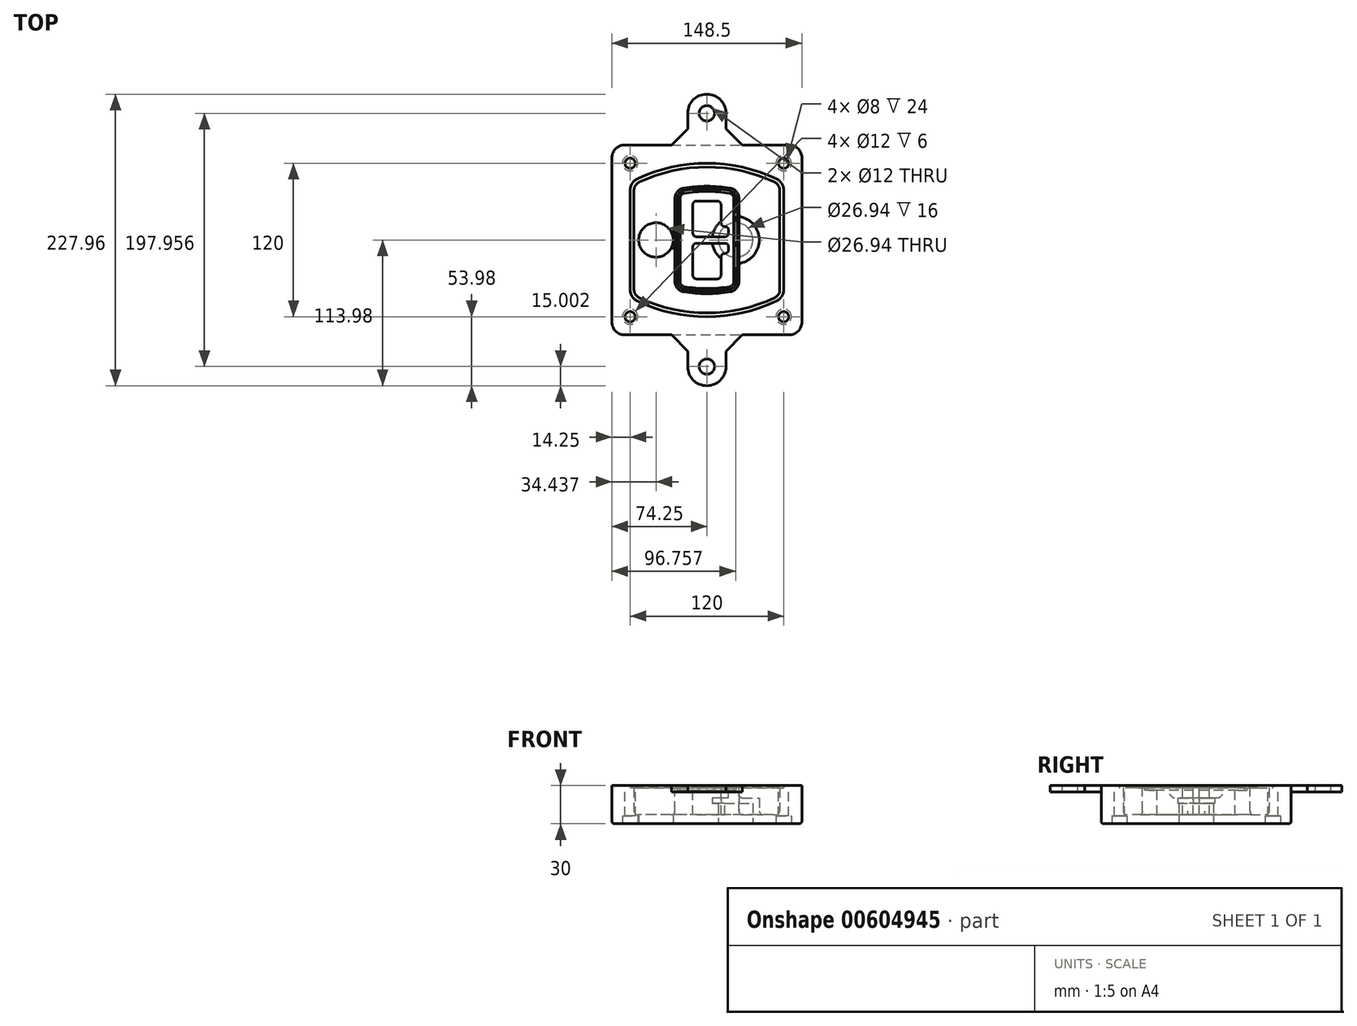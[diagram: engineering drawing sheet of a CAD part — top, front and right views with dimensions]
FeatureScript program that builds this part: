
annotation { "Feature Type Name" : "Feature", "Feature Type Description" : "" }
export const myFeature = defineFeature(function(context is Context, id is Id, definition is map)
    precondition{}
    {
        {
            var Q0;
            Q0=qCreatedBy(makeId("Top.planeOp"),FACE);
            var sketch = newSketch(context, id + "F0", { "sketchPlane" : qUnion([Q0])});
            skPoint(sketch, "E0.rect.middle", {"position": v(0, 0) * mm});
            skLineSegment(sketch, "E1.bottom", {"start": v(-64.25, -74.25) * mm, "end": v(64.25, -74.25) * mm});
            skLineSegment(sketch, "E1.top", {"start": v(-64.25, 74.25) * mm, "end": v(64.25, 74.25) * mm});
            skLineSegment(sketch, "E1.left", {"start": v(-74.25, -64.25) * mm, "end": v(-74.25, 64.25) * mm});
            skLineSegment(sketch, "E1.right", {"start": v(74.25, -64.25) * mm, "end": v(74.25, 64.25) * mm});
            skLineSegment(sketch, "E2", {"start": v(-74.25, 74.25) * mm, "end": v(74.25, -74.25) * mm, "construction": true});
            skLineSegment(sketch, "E3", {"start": v(74.25, 74.25) * mm, "end": v(-74.25, -74.25) * mm, "construction": true});
            skCircle(sketch, "E4", {"center": v(-60, 60) * mm, "radius": 4 * mm});
            skCircle(sketch, "E5", {"center": v(60, 60) * mm, "radius": 4 * mm});
            skCircle(sketch, "E6", {"center": v(60, -60) * mm, "radius": 4 * mm});
            skCircle(sketch, "E7", {"center": v(-60, -60) * mm, "radius": 4 * mm});
            skLineSegment(sketch, "E8", {"start": v(-60, 60) * mm, "end": v(60, 60) * mm, "construction": true});
            skLineSegment(sketch, "E9", {"start": v(60, 60) * mm, "end": v(60, -60) * mm, "construction": true});
            skLineSegment(sketch, "E10", {"start": v(60, -60) * mm, "end": v(-60, -60) * mm, "construction": true});
            skLineSegment(sketch, "E11", {"start": v(-60, -60) * mm, "end": v(-60, 60) * mm, "construction": true});
            skLineSegment(sketch, "E12", {"start": v(-60, 38.83) * mm, "end": v(-60, -38.83) * mm});
            skLineSegment(sketch, "E13", {"start": v(60, 38.83) * mm, "end": v(60, -38.83) * mm});
            skArc(sketch, "E14", {"start": v(54.26, 47.88) * mm, "mid": v(0, 60) * mm, "end": v(-54.26, 47.88) * mm});
            skArc(sketch, "E15", {"start": v(-54.26, -47.88) * mm, "mid": v(0, -60) * mm, "end": v(54.26, -47.88) * mm});
            skLineSegment(sketch, "E16", {"start": v(-60, 0) * mm, "end": v(60, 0) * mm, "construction": true});
            skPoint(sketch, "E17.visualSharp", {"position": v(-60, -45) * mm});
            skArc(sketch, "E17.filletArc", {"start": v(-60, -38.83) * mm, "mid": v(-58.44, -44.2) * mm, "end": v(-54.26, -47.88) * mm});
            skPoint(sketch, "E18.visualSharp", {"position": v(-60, 45) * mm});
            skArc(sketch, "E18.filletArc", {"start": v(-54.26, 47.88) * mm, "mid": v(-58.44, 44.2) * mm, "end": v(-60, 38.83) * mm});
            skPoint(sketch, "E19.visualSharp", {"position": v(60, 45) * mm});
            skArc(sketch, "E19.filletArc", {"start": v(60, 38.83) * mm, "mid": v(58.44, 44.2) * mm, "end": v(54.26, 47.88) * mm});
            skPoint(sketch, "E20.visualSharp", {"position": v(60, -45) * mm});
            skArc(sketch, "E20.filletArc", {"start": v(54.26, -47.88) * mm, "mid": v(58.44, -44.2) * mm, "end": v(60, -38.83) * mm});
            skPoint(sketch, "E21.visualSharp", {"position": v(-74.25, 74.25) * mm});
            skArc(sketch, "E21.filletArc", {"start": v(-64.25, 74.25) * mm, "mid": v(-71.32, 71.32) * mm, "end": v(-74.25, 64.25) * mm});
            skPoint(sketch, "E22.visualSharp", {"position": v(74.25, 74.25) * mm});
            skArc(sketch, "E22.filletArc", {"start": v(74.25, 64.25) * mm, "mid": v(71.32, 71.32) * mm, "end": v(64.25, 74.25) * mm});
            skPoint(sketch, "E23.visualSharp", {"position": v(74.25, -74.25) * mm});
            skArc(sketch, "E23.filletArc", {"start": v(64.25, -74.25) * mm, "mid": v(71.32, -71.32) * mm, "end": v(74.25, -64.25) * mm});
            skPoint(sketch, "E24.visualSharp", {"position": v(-74.25, -74.25) * mm});
            skArc(sketch, "E24.filletArc", {"start": v(-74.25, -64.25) * mm, "mid": v(-71.32, -71.32) * mm, "end": v(-64.25, -74.25) * mm});
            skArc(sketch, "E25.0", {"start": v(57, 38.83) * mm, "mid": v(55.9, 42.58) * mm, "end": v(52.98, 45.17) * mm});
            skLineSegment(sketch, "E25.1", {"start": v(57, 38.83) * mm, "end": v(57, -38.83) * mm});
            skArc(sketch, "E25.2", {"start": v(52.98, -45.17) * mm, "mid": v(55.9, -42.58) * mm, "end": v(57, -38.83) * mm});
            skArc(sketch, "E25.3", {"start": v(-52.98, -45.17) * mm, "mid": v(0, -57) * mm, "end": v(52.98, -45.17) * mm});
            skArc(sketch, "E25.4", {"start": v(-57, -38.83) * mm, "mid": v(-55.9, -42.58) * mm, "end": v(-52.98, -45.17) * mm});
            skArc(sketch, "E25.5", {"start": v(52.98, 45.17) * mm, "mid": v(0, 57) * mm, "end": v(-52.98, 45.17) * mm});
            skLineSegment(sketch, "E25.6", {"start": v(-57, 38.83) * mm, "end": v(-57, -38.83) * mm});
            skArc(sketch, "E25.7", {"start": v(-52.98, 45.17) * mm, "mid": v(-55.9, 42.58) * mm, "end": v(-57, 38.83) * mm});
            skArc(sketch, "E26.0", {"start": v(-55.96, 51.5) * mm, "mid": v(-61.82, 46.33) * mm, "end": v(-64, 38.83) * mm});
            skArc(sketch, "E26.1", {"start": v(55.96, 51.5) * mm, "mid": v(0, 64) * mm, "end": v(-55.96, 51.5) * mm});
            skArc(sketch, "E26.2", {"start": v(64, 38.83) * mm, "mid": v(61.82, 46.33) * mm, "end": v(55.96, 51.5) * mm});
            skLineSegment(sketch, "E26.3", {"start": v(64, 38.83) * mm, "end": v(64, -38.83) * mm});
            skArc(sketch, "E26.4", {"start": v(55.96, -51.5) * mm, "mid": v(61.82, -46.33) * mm, "end": v(64, -38.83) * mm});
            skLineSegment(sketch, "E26.5", {"start": v(-64, 38.83) * mm, "end": v(-64, -38.83) * mm});
            skArc(sketch, "E26.6", {"start": v(-55.96, -51.5) * mm, "mid": v(0, -64) * mm, "end": v(55.96, -51.5) * mm});
            skArc(sketch, "E26.7", {"start": v(-64, -38.83) * mm, "mid": v(-61.82, -46.33) * mm, "end": v(-55.96, -51.5) * mm});
            skSolve(sketch);
        }
        {
            var Q0;
            Q0=makeQuery(id+"F0.imprint","IMPRINT",FACE,{"disambiguationData":[TD([[makeQuery(id+"F0.imprint","IMPRINT",EDGE,{"derivedFrom":sQuery(id+"F0.wireOp",EDGE,"E1.bottom")}),1.0]])]});
            var Q1;
            Q1=makeQuery(id+"F0.imprint","IMPRINT",FACE,{"disambiguationData":[TD([[makeQuery(id+"F0.imprint","IMPRINT",EDGE,{"derivedFrom":sQuery(id+"F0.wireOp",EDGE,"E12")}),1.0]])]});
            var Q2;
            Q2=makeQuery(id+"F0.imprint","IMPRINT",FACE,{"disambiguationData":[TD([[makeQuery(id+"F0.imprint","IMPRINT",EDGE,{"derivedFrom":sQuery(id+"F0.wireOp",EDGE,"E25.0")}),1.0]])]});
            var Q3;
            Q3=makeQuery(id+"F0.imprint","IMPRINT",FACE,{"disambiguationData":[TD([[makeQuery(id+"F0.imprint","IMPRINT",EDGE,{"derivedFrom":sQuery(id+"F0.wireOp",EDGE,"E12")}),-1.0]])]});
            extrude(context, id + "F1", {"entities" : qUnion([Q0, Q1, Q2, Q3]), "oppositeDirection" : true, "depth" : 25 * mm});
        }
        {
            var Q0;
            Q0=makeQuery(id+"F0.imprint","IMPRINT",FACE,{"disambiguationData":[TD([[makeQuery(id+"F0.imprint","IMPRINT",EDGE,{"derivedFrom":sQuery(id+"F0.wireOp",EDGE,"E12")}),1.0]])]});
            extrude(context, id + "F2", {"entities" : qUnion([Q0]), "operationType" : NewBodyOperationType.ADD, "depth" : 3 * mm});
        }
        {
            var Q0;
            Q0=makeQuery(id+"F0.imprint","IMPRINT",FACE,{"disambiguationData":[TD([[makeQuery(id+"F0.imprint","IMPRINT",EDGE,{"derivedFrom":sQuery(id+"F0.wireOp",EDGE,"E25.0")}),1.0]])]});
            extrude(context, id + "F3", {"entities" : qUnion([Q0]), "operationType" : NewBodyOperationType.REMOVE, "oppositeDirection" : true, "depth" : 18 * mm});
        }
        {
            var Q0;
            Q0=makeQuery(id+"F2.opExtrude","CAP_FACE",FACE,{"disambiguationData":[OSD([sQuery(id+"F0.wireOp",EDGE,"E12"),sQuery(id+"F0.wireOp",EDGE,"E13"),sQuery(id+"F0.wireOp",EDGE,"E14"),sQuery(id+"F0.wireOp",EDGE,"E15"),sQuery(id+"F0.wireOp",EDGE,"E17.filletArc"),sQuery(id+"F0.wireOp",EDGE,"E18.filletArc"),sQuery(id+"F0.wireOp",EDGE,"E19.filletArc"),sQuery(id+"F0.wireOp",EDGE,"E20.filletArc"),sQuery(id+"F0.wireOp",EDGE,"E25.0"),sQuery(id+"F0.wireOp",EDGE,"E25.1"),sQuery(id+"F0.wireOp",EDGE,"E25.2"),sQuery(id+"F0.wireOp",EDGE,"E25.3"),sQuery(id+"F0.wireOp",EDGE,"E25.4"),sQuery(id+"F0.wireOp",EDGE,"E25.5"),sQuery(id+"F0.wireOp",EDGE,"E25.6"),sQuery(id+"F0.wireOp",EDGE,"E25.7")])],"isStart":false});
            var sketch = newSketch(context, id + "F4", { "sketchPlane" : qUnion([Q0])});
            skArc(sketch, "E27.0", {"start": v(-18.34, -40.45) * mm, "mid": v(0, -42) * mm, "end": v(18.34, -40.45) * mm});
            skArc(sketch, "E28.0", {"start": v(18.34, 40.45) * mm, "mid": v(0, 42) * mm, "end": v(-18.34, 40.45) * mm});
            skLineSegment(sketch, "E29", {"start": v(-25, 32.57) * mm, "end": v(-25, -32.57) * mm});
            skLineSegment(sketch, "E30", {"start": v(25, 32.57) * mm, "end": v(25, -32.57) * mm});
            skLineSegment(sketch, "E31", {"start": v(-25, 39.1) * mm, "end": v(25, 39.1) * mm, "construction": true});
            skLineSegment(sketch, "E32", {"start": v(-25, -39.1) * mm, "end": v(25, -39.1) * mm, "construction": true});
            skPoint(sketch, "E33.visualSharp", {"position": v(-25, 39.1) * mm});
            skArc(sketch, "E33.filletArc", {"start": v(-18.34, 40.45) * mm, "mid": v(-23.11, 37.73) * mm, "end": v(-25, 32.57) * mm});
            skPoint(sketch, "E34.visualSharp", {"position": v(25, 39.1) * mm});
            skArc(sketch, "E34.filletArc", {"start": v(25, 32.57) * mm, "mid": v(23.11, 37.73) * mm, "end": v(18.34, 40.45) * mm});
            skPoint(sketch, "E35.visualSharp", {"position": v(25, -39.1) * mm});
            skArc(sketch, "E35.filletArc", {"start": v(18.34, -40.45) * mm, "mid": v(23.11, -37.73) * mm, "end": v(25, -32.57) * mm});
            skPoint(sketch, "E36.visualSharp", {"position": v(-25, -39.1) * mm});
            skArc(sketch, "E36.filletArc", {"start": v(-25, -32.57) * mm, "mid": v(-23.11, -37.73) * mm, "end": v(-18.34, -40.45) * mm});
            skArc(sketch, "E37.0", {"start": v(52.98, 45.17) * mm, "mid": v(0, 57) * mm, "end": v(-52.98, 45.17) * mm});
            skArc(sketch, "E37.1", {"start": v(-52.98, 45.17) * mm, "mid": v(-55.9, 42.58) * mm, "end": v(-57, 38.83) * mm});
            skLineSegment(sketch, "E37.2", {"start": v(-57, 38.83) * mm, "end": v(-57, -38.83) * mm});
            skArc(sketch, "E37.3", {"start": v(-57, -38.83) * mm, "mid": v(-55.9, -42.58) * mm, "end": v(-52.98, -45.17) * mm});
            skArc(sketch, "E37.4", {"start": v(-52.98, -45.17) * mm, "mid": v(0, -57) * mm, "end": v(52.98, -45.17) * mm});
            skArc(sketch, "E37.5", {"start": v(52.98, -45.17) * mm, "mid": v(55.9, -42.58) * mm, "end": v(57, -38.83) * mm});
            skLineSegment(sketch, "E37.6", {"start": v(57, 38.83) * mm, "end": v(57, -38.83) * mm});
            skArc(sketch, "E37.7", {"start": v(57, 38.83) * mm, "mid": v(55.9, 42.58) * mm, "end": v(52.98, 45.17) * mm});
            skLineSegment(sketch, "E38.0", {"start": v(23, 32.57) * mm, "end": v(23, -32.57) * mm});
            skArc(sketch, "E38.1", {"start": v(18, -38.48) * mm, "mid": v(21.58, -36.44) * mm, "end": v(23, -32.57) * mm});
            skArc(sketch, "E38.2", {"start": v(-18, -38.48) * mm, "mid": v(0, -40) * mm, "end": v(18, -38.48) * mm});
            skArc(sketch, "E38.3", {"start": v(-23, -32.57) * mm, "mid": v(-21.58, -36.44) * mm, "end": v(-18, -38.48) * mm});
            skLineSegment(sketch, "E38.4", {"start": v(-23, 32.57) * mm, "end": v(-23, -32.57) * mm});
            skArc(sketch, "E38.5", {"start": v(23, 32.57) * mm, "mid": v(21.58, 36.44) * mm, "end": v(18, 38.48) * mm});
            skArc(sketch, "E38.6", {"start": v(-18, 38.48) * mm, "mid": v(-21.58, 36.44) * mm, "end": v(-23, 32.57) * mm});
            skArc(sketch, "E38.7", {"start": v(18, 38.48) * mm, "mid": v(0, 40) * mm, "end": v(-18, 38.48) * mm});
            skArc(sketch, "E39.0", {"start": v(21, 32.57) * mm, "mid": v(20.06, 35.15) * mm, "end": v(17.67, 36.5) * mm});
            skLineSegment(sketch, "E39.1", {"start": v(21, 32.57) * mm, "end": v(21, -32.57) * mm});
            skArc(sketch, "E39.2", {"start": v(17.67, -36.5) * mm, "mid": v(20.06, -35.15) * mm, "end": v(21, -32.57) * mm});
            skArc(sketch, "E39.3", {"start": v(-17.67, -36.5) * mm, "mid": v(0, -38) * mm, "end": v(17.67, -36.5) * mm});
            skArc(sketch, "E39.4", {"start": v(-21, -32.57) * mm, "mid": v(-20.06, -35.15) * mm, "end": v(-17.67, -36.5) * mm});
            skArc(sketch, "E39.5", {"start": v(17.67, 36.5) * mm, "mid": v(0, 38) * mm, "end": v(-17.67, 36.5) * mm});
            skLineSegment(sketch, "E39.6", {"start": v(-21, 32.57) * mm, "end": v(-21, -32.57) * mm});
            skArc(sketch, "E39.7", {"start": v(-17.67, 36.5) * mm, "mid": v(-20.06, 35.15) * mm, "end": v(-21, 32.57) * mm});
            skLineSegment(sketch, "E40", {"start": v(-25, 0) * mm, "end": v(25, 0) * mm, "construction": true});
            skLineSegment(sketch, "E41", {"start": v(-11, 5.5) * mm, "end": v(-11, 27.5) * mm});
            skLineSegment(sketch, "E42", {"start": v(-8, 30.5) * mm, "end": v(8, 30.5) * mm});
            skLineSegment(sketch, "E43", {"start": v(11, 27.5) * mm, "end": v(11, 13.5) * mm});
            skLineSegment(sketch, "E44", {"start": v(14, 10.5) * mm, "end": v(14, 10.5) * mm});
            skLineSegment(sketch, "E45", {"start": v(17, 7.5) * mm, "end": v(17, 5.5) * mm});
            skLineSegment(sketch, "E46", {"start": v(14, 2.5) * mm, "end": v(-8, 2.5) * mm});
            skPoint(sketch, "E47.visualSharp", {"position": v(-11, 30.5) * mm});
            skArc(sketch, "E47.filletArc", {"start": v(-8, 30.5) * mm, "mid": v(-10.12, 29.62) * mm, "end": v(-11, 27.5) * mm});
            skPoint(sketch, "E48.visualSharp", {"position": v(11, 30.5) * mm});
            skArc(sketch, "E48.filletArc", {"start": v(11, 27.5) * mm, "mid": v(10.12, 29.62) * mm, "end": v(8, 30.5) * mm});
            skPoint(sketch, "E49.visualSharp", {"position": v(11, 10.5) * mm});
            skArc(sketch, "E49.filletArc", {"start": v(11, 13.5) * mm, "mid": v(11.88, 11.38) * mm, "end": v(14, 10.5) * mm});
            skPoint(sketch, "E50.visualSharp", {"position": v(17, 10.5) * mm});
            skArc(sketch, "E50.filletArc", {"start": v(17, 7.5) * mm, "mid": v(16.12, 9.62) * mm, "end": v(14, 10.5) * mm});
            skPoint(sketch, "E51.visualSharp", {"position": v(17, 2.5) * mm});
            skArc(sketch, "E51.filletArc", {"start": v(14, 2.5) * mm, "mid": v(16.12, 3.38) * mm, "end": v(17, 5.5) * mm});
            skPoint(sketch, "E52.visualSharp", {"position": v(-11, 2.5) * mm});
            skArc(sketch, "E52.filletArc", {"start": v(-11, 5.5) * mm, "mid": v(-10.12, 3.38) * mm, "end": v(-8, 2.5) * mm});
            skLineSegment(sketch, "E53.0.MirrorCS", {"start": v(14, -2.5) * mm, "end": v(-8, -2.5) * mm});
            skArc(sketch, "E54.0.MirrorCS", {"start": v(-11, -5.5) * mm, "mid": v(-10.12, -3.38) * mm, "end": v(-8, -2.5) * mm});
            skLineSegment(sketch, "E55.0.MirrorCS", {"start": v(-11, -5.5) * mm, "end": v(-11, -27.5) * mm});
            skArc(sketch, "E56.0.MirrorCS", {"start": v(-8, -30.5) * mm, "mid": v(-10.12, -29.62) * mm, "end": v(-11, -27.5) * mm});
            skLineSegment(sketch, "E57.0.MirrorCS", {"start": v(-8, -30.5) * mm, "end": v(8, -30.5) * mm});
            skArc(sketch, "E58.0.MirrorCS", {"start": v(11, -27.5) * mm, "mid": v(10.12, -29.62) * mm, "end": v(8, -30.5) * mm});
            skLineSegment(sketch, "E59.0.MirrorCS", {"start": v(11, -27.5) * mm, "end": v(11, -13.5) * mm});
            skArc(sketch, "E60.0.MirrorCS", {"start": v(11, -13.5) * mm, "mid": v(11.88, -11.38) * mm, "end": v(14, -10.5) * mm});
            skArc(sketch, "E61.0.MirrorCS", {"start": v(17, -7.5) * mm, "mid": v(16.12, -9.62) * mm, "end": v(14, -10.5) * mm});
            skLineSegment(sketch, "E62.0.MirrorCS", {"start": v(17, -7.5) * mm, "end": v(17, -5.5) * mm});
            skArc(sketch, "E63.0.MirrorCS", {"start": v(14, -2.5) * mm, "mid": v(16.12, -3.38) * mm, "end": v(17, -5.5) * mm});
            skSolve(sketch);
        }
        {
            var Q0;
            Q0=makeQuery(id+"F4.imprint","IMPRINT",FACE,{"disambiguationData":[TD([[makeQuery(id+"F4.imprint","IMPRINT",EDGE,{"derivedFrom":sQuery(id+"F4.wireOp",EDGE,"E27.0")}),1.0]])]});
            var Q1;
            Q1=makeQuery(id+"F4.imprint","IMPRINT",FACE,{"disambiguationData":[TD([[makeQuery(id+"F4.imprint","IMPRINT",EDGE,{"derivedFrom":sQuery(id+"F4.wireOp",EDGE,"E38.0")}),-1.0]])]});
            var Q2;
            Q2=makeQuery(id+"F4.imprint","IMPRINT",FACE,{"disambiguationData":[TD([[makeQuery(id+"F4.imprint","IMPRINT",EDGE,{"derivedFrom":sQuery(id+"F4.wireOp",EDGE,"E39.0")}),1.0]])]});
            extrude(context, id + "F5", {"entities" : qUnion([Q0, Q1, Q2]), "operationType" : NewBodyOperationType.ADD, "endBound" : BoundingType.UP_TO_NEXT, "oppositeDirection" : true, "depth" : 25 * mm, "offsetDistance" : 25 * mm});
        }
        {
            var Q0;
            Q0=makeQuery(id+"F4.imprint","IMPRINT",FACE,{"disambiguationData":[TD([[makeQuery(id+"F4.imprint","IMPRINT",EDGE,{"derivedFrom":sQuery(id+"F4.wireOp",EDGE,"E38.0")}),-1.0]])]});
            extrude(context, id + "F6", {"entities" : qUnion([Q0]), "operationType" : NewBodyOperationType.REMOVE, "oppositeDirection" : true, "depth" : 2 * mm, "offsetDistance" : 25 * mm});
        }
        {
            var Q0;
            Q0=makeQuery(id+"F1.opExtrude","CAP_FACE",FACE,{"disambiguationData":[OSD([sQuery(id+"F0.wireOp",EDGE,"E1.bottom"),sQuery(id+"F0.wireOp",EDGE,"E1.top"),sQuery(id+"F0.wireOp",EDGE,"E1.left"),sQuery(id+"F0.wireOp",EDGE,"E1.right"),sQuery(id+"F0.wireOp",EDGE,"E4"),sQuery(id+"F0.wireOp",EDGE,"E5"),sQuery(id+"F0.wireOp",EDGE,"E6"),sQuery(id+"F0.wireOp",EDGE,"E7"),sQuery(id+"F0.wireOp",EDGE,"E21.filletArc"),sQuery(id+"F0.wireOp",EDGE,"E22.filletArc"),sQuery(id+"F0.wireOp",EDGE,"E23.filletArc"),sQuery(id+"F0.wireOp",EDGE,"E24.filletArc")])],"isStart":false});
            var sketch = newSketch(context, id + "F7", { "sketchPlane" : qUnion([Q0])});
            skCircle(sketch, "E64", {"center": v(22.5, 0) * mm, "radius": 13.47 * mm});
            skCircle(sketch, "E65", {"center": v(-39.81, 0) * mm, "radius": 13.47 * mm});
            skLineSegment(sketch, "E66", {"start": v(74.25, 0) * mm, "end": v(-74.25, 0) * mm});
            skCircle(sketch, "E67", {"center": v(22.5, 0) * mm, "radius": 18.47 * mm});
            skCircle(sketch, "E68", {"center": v(60, -60) * mm, "radius": 6 * mm});
            skCircle(sketch, "E69", {"center": v(-60, -60) * mm, "radius": 6 * mm});
            skCircle(sketch, "E70", {"center": v(-60, 60) * mm, "radius": 6 * mm});
            skCircle(sketch, "E71", {"center": v(60, 60) * mm, "radius": 6 * mm});
            skSolve(sketch);
        }
        {
            var Q0;
            {var subQ1=sQuery(id+"F7.wireOp",EDGE,"E66");var subQ4=sQuery(id+"F7.wireOp",EDGE,"E64");var subQ6=makeQuery(id+"F7.imprint","INTERSECT",VERTEX,{"disambiguationData":[OD(0.0)],"derivedFrom":[subQ4,subQ1]});Q0=makeQuery(id+"F7.imprint","IMPRINT",FACE,{"disambiguationData":[TD([[makeQuery(id+"F7.imprint","IMPRINT",EDGE,{"disambiguationData":[TD([[subQ6,-1.0]])],"derivedFrom":subQ4}),-1.0]])]});}
            var Q1;
            {var subQ0=sQuery(id+"F7.wireOp",EDGE,"E66");var subQ1=sQuery(id+"F7.wireOp",EDGE,"E64");var subQ3=makeQuery(id+"F7.imprint","INTERSECT",VERTEX,{"disambiguationData":[OD(0.0)],"derivedFrom":[subQ1,subQ0]});Q1=makeQuery(id+"F7.imprint","IMPRINT",FACE,{"disambiguationData":[TD([[makeQuery(id+"F7.imprint","IMPRINT",EDGE,{"disambiguationData":[TD([[subQ3,-1.0]])],"derivedFrom":subQ1}),1.0]])]});}
            var Q2;
            {var subQ0=sQuery(id+"F7.wireOp",EDGE,"E66");var subQ1=sQuery(id+"F7.wireOp",EDGE,"E64");var subQ3=makeQuery(id+"F7.imprint","INTERSECT",VERTEX,{"disambiguationData":[OD(0.0)],"derivedFrom":[subQ1,subQ0]});Q2=makeQuery(id+"F7.imprint","IMPRINT",FACE,{"disambiguationData":[TD([[makeQuery(id+"F7.imprint","IMPRINT",EDGE,{"disambiguationData":[TD([[subQ3,1.0]])],"derivedFrom":subQ1}),1.0]])]});}
            var Q3;
            {var subQ1=sQuery(id+"F7.wireOp",EDGE,"E66");var subQ4=sQuery(id+"F7.wireOp",EDGE,"E64");var subQ6=makeQuery(id+"F7.imprint","INTERSECT",VERTEX,{"disambiguationData":[OD(0.0)],"derivedFrom":[subQ4,subQ1]});Q3=makeQuery(id+"F7.imprint","IMPRINT",FACE,{"disambiguationData":[TD([[makeQuery(id+"F7.imprint","IMPRINT",EDGE,{"disambiguationData":[TD([[subQ6,1.0]])],"derivedFrom":subQ4}),-1.0]])]});}
            extrude(context, id + "F8", {"entities" : qUnion([Q0, Q1, Q2, Q3]), "operationType" : NewBodyOperationType.ADD, "oppositeDirection" : true, "depth" : 20 * mm});
        }
        {
            var Q0;
            {var subQ0=sQuery(id+"F7.wireOp",EDGE,"E66");var subQ1=sQuery(id+"F7.wireOp",EDGE,"E64");var subQ3=makeQuery(id+"F7.imprint","INTERSECT",VERTEX,{"disambiguationData":[OD(0.0)],"derivedFrom":[subQ1,subQ0]});Q0=makeQuery(id+"F7.imprint","IMPRINT",FACE,{"disambiguationData":[TD([[makeQuery(id+"F7.imprint","IMPRINT",EDGE,{"disambiguationData":[TD([[subQ3,-1.0]])],"derivedFrom":subQ1}),1.0]])]});}
            var Q1;
            {var subQ0=sQuery(id+"F7.wireOp",EDGE,"E66");var subQ1=sQuery(id+"F7.wireOp",EDGE,"E64");var subQ3=makeQuery(id+"F7.imprint","INTERSECT",VERTEX,{"disambiguationData":[OD(0.0)],"derivedFrom":[subQ1,subQ0]});Q1=makeQuery(id+"F7.imprint","IMPRINT",FACE,{"disambiguationData":[TD([[makeQuery(id+"F7.imprint","IMPRINT",EDGE,{"disambiguationData":[TD([[subQ3,1.0]])],"derivedFrom":subQ1}),1.0]])]});}
            extrude(context, id + "F9", {"entities" : qUnion([Q0, Q1]), "operationType" : NewBodyOperationType.REMOVE, "oppositeDirection" : true, "depth" : 16 * mm});
        }
        {
            var Q0;
            {var subQ0=sQuery(id+"F7.wireOp",EDGE,"E66");var subQ1=sQuery(id+"F7.wireOp",EDGE,"E65");var subQ3=makeQuery(id+"F7.imprint","INTERSECT",VERTEX,{"disambiguationData":[OD(0.0)],"derivedFrom":[subQ1,subQ0]});Q0=makeQuery(id+"F7.imprint","IMPRINT",FACE,{"disambiguationData":[TD([[makeQuery(id+"F7.imprint","IMPRINT",EDGE,{"disambiguationData":[TD([[subQ3,-1.0]])],"derivedFrom":subQ1}),1.0]])]});}
            var Q1;
            {var subQ0=sQuery(id+"F7.wireOp",EDGE,"E66");var subQ1=sQuery(id+"F7.wireOp",EDGE,"E65");var subQ3=makeQuery(id+"F7.imprint","INTERSECT",VERTEX,{"disambiguationData":[OD(0.0)],"derivedFrom":[subQ1,subQ0]});Q1=makeQuery(id+"F7.imprint","IMPRINT",FACE,{"disambiguationData":[TD([[makeQuery(id+"F7.imprint","IMPRINT",EDGE,{"disambiguationData":[TD([[subQ3,1.0]])],"derivedFrom":subQ1}),1.0]])]});}
            extrude(context, id + "F10", {"entities" : qUnion([Q0, Q1]), "operationType" : NewBodyOperationType.REMOVE, "oppositeDirection" : true, "depth" : 25 * mm});
        }
        {
            var Q0;
            Q0=makeQuery(id+"F7.imprint","IMPRINT",FACE,{"disambiguationData":[TD([[makeQuery(id+"F7.imprint","IMPRINT",EDGE,{"derivedFrom":sQuery(id+"F7.wireOp",EDGE,"E68")}),1.0]])]});
            var Q1;
            Q1=makeQuery(id+"F7.imprint","IMPRINT",FACE,{"disambiguationData":[TD([[makeQuery(id+"F7.imprint","IMPRINT",EDGE,{"derivedFrom":makeQuery(id+"F1.opExtrude","CAP_EDGE",EDGE,{"disambiguationData":[OSD([sQuery(id+"F0.wireOp",EDGE,"E5")])],"isStart":false})}),-1.0]])]});
            var Q2;
            Q2=makeQuery(id+"F7.imprint","IMPRINT",FACE,{"disambiguationData":[TD([[makeQuery(id+"F7.imprint","IMPRINT",EDGE,{"derivedFrom":sQuery(id+"F7.wireOp",EDGE,"E69")}),1.0]])]});
            var Q3;
            Q3=makeQuery(id+"F7.imprint","IMPRINT",FACE,{"disambiguationData":[TD([[makeQuery(id+"F7.imprint","IMPRINT",EDGE,{"derivedFrom":makeQuery(id+"F1.opExtrude","CAP_EDGE",EDGE,{"disambiguationData":[OSD([sQuery(id+"F0.wireOp",EDGE,"E4")])],"isStart":false})}),-1.0]])]});
            var Q4;
            Q4=makeQuery(id+"F7.imprint","IMPRINT",FACE,{"disambiguationData":[TD([[makeQuery(id+"F7.imprint","IMPRINT",EDGE,{"derivedFrom":sQuery(id+"F7.wireOp",EDGE,"E70")}),1.0]])]});
            var Q5;
            Q5=makeQuery(id+"F7.imprint","IMPRINT",FACE,{"disambiguationData":[TD([[makeQuery(id+"F7.imprint","IMPRINT",EDGE,{"derivedFrom":makeQuery(id+"F1.opExtrude","CAP_EDGE",EDGE,{"disambiguationData":[OSD([sQuery(id+"F0.wireOp",EDGE,"E7")])],"isStart":false})}),-1.0]])]});
            var Q6;
            Q6=makeQuery(id+"F7.imprint","IMPRINT",FACE,{"disambiguationData":[TD([[makeQuery(id+"F7.imprint","IMPRINT",EDGE,{"derivedFrom":sQuery(id+"F7.wireOp",EDGE,"E71")}),1.0]])]});
            var Q7;
            Q7=makeQuery(id+"F7.imprint","IMPRINT",FACE,{"disambiguationData":[TD([[makeQuery(id+"F7.imprint","IMPRINT",EDGE,{"derivedFrom":makeQuery(id+"F1.opExtrude","CAP_EDGE",EDGE,{"disambiguationData":[OSD([sQuery(id+"F0.wireOp",EDGE,"E6")])],"isStart":false})}),-1.0]])]});
            extrude(context, id + "F11", {"entities" : qUnion([Q0, Q1, Q2, Q3, Q4, Q5, Q6, Q7]), "operationType" : NewBodyOperationType.REMOVE, "oppositeDirection" : true, "depth" : 6 * mm});
        }
        {
            var Q0;
            Q0=makeQuery(id+"F9.boolean.opBoolean","COPY",FACE,{"derivedFrom":makeQuery(id+"F9.opExtrude","CAP_FACE",FACE,{"disambiguationData":[OSD([sQuery(id+"F7.wireOp",EDGE,"E64")])],"isStart":false})});
            var sketch = newSketch(context, id + "F12", { "sketchPlane" : qUnion([Q0])});
            skArc(sketch, "E72.0", {"start": v(11, 14.45) * mm, "mid": v(6.45, 9.13) * mm, "end": v(4.2, 2.5) * mm});
            skArc(sketch, "E72.1", {"start": v(4.2, -2.5) * mm, "mid": v(6.45, -9.13) * mm, "end": v(11, -14.45) * mm});
            skLineSegment(sketch, "E73", {"start": v(4.2, -2.5) * mm, "end": v(14, -2.5) * mm});
            skLineSegment(sketch, "E74.0", {"start": v(14, 2.5) * mm, "end": v(4.2, 2.5) * mm});
            skArc(sketch, "E74.1", {"start": v(14, 2.5) * mm, "mid": v(16.12, 3.38) * mm, "end": v(17, 5.5) * mm});
            skLineSegment(sketch, "E74.2", {"start": v(17, 7.5) * mm, "end": v(17, 5.5) * mm});
            skArc(sketch, "E74.3", {"start": v(17, 7.5) * mm, "mid": v(16.12, 9.62) * mm, "end": v(14, 10.5) * mm});
            skArc(sketch, "E74.4", {"start": v(11, 13.5) * mm, "mid": v(11.88, 11.38) * mm, "end": v(14, 10.5) * mm});
            skLineSegment(sketch, "E74.5", {"start": v(11, 14.45) * mm, "end": v(11, 13.5) * mm});
            skLineSegment(sketch, "E74.7", {"start": v(14, -2.5) * mm, "end": v(4.2, -2.5) * mm});
            skArc(sketch, "E74.8", {"start": v(14, -2.5) * mm, "mid": v(16.12, -3.38) * mm, "end": v(17, -5.5) * mm});
            skLineSegment(sketch, "E74.9", {"start": v(17, -7.5) * mm, "end": v(17, -5.5) * mm});
            skArc(sketch, "E74.10", {"start": v(17, -7.5) * mm, "mid": v(16.12, -9.62) * mm, "end": v(14, -10.5) * mm});
            skArc(sketch, "E74.11", {"start": v(11, -13.5) * mm, "mid": v(11.88, -11.38) * mm, "end": v(14, -10.5) * mm});
            skLineSegment(sketch, "E74.12", {"start": v(11, -14.45) * mm, "end": v(11, -13.5) * mm});
            skPoint(sketch, "E75.orphan", {"position": v(11, -27.5) * mm});
            skPoint(sketch, "E76.orphan", {"position": v(-8, -2.5) * mm});
            skPoint(sketch, "E77.orphan", {"position": v(-8, 2.5) * mm});
            skPoint(sketch, "E78.orphan", {"position": v(11, 27.5) * mm});
            skSolve(sketch);
        }
        {
            var Q0;
            {var subQ7=sQuery(id+"F12.wireOp",EDGE,"E72.0");var subQ14=sQuery(id+"F12.wireOp",EDGE,"E72.1");var subQ16=sQuery(id+"F12.wireOp",EDGE,"E74.1");var subQ18=sQuery(id+"F12.wireOp",EDGE,"E74.8");Q0=qUnion([makeQuery(id+"F12.imprint","IMPRINT",FACE,{"disambiguationData":[TD([[makeQuery(id+"F12.imprint","IMPRINT",EDGE,{"derivedFrom":subQ7}),1.0]])]}),makeQuery(id+"F12.imprint","IMPRINT",FACE,{"disambiguationData":[TD([[makeQuery(id+"F12.imprint","IMPRINT",EDGE,{"derivedFrom":subQ14}),1.0]])]}),makeQuery(id+"F12.imprint","IMPRINT",FACE,{"disambiguationData":[TD([[makeQuery(id+"F12.imprint","IMPRINT",EDGE,{"derivedFrom":subQ16}),1.0]])]}),makeQuery(id+"F12.imprint","IMPRINT",FACE,{"disambiguationData":[TD([[makeQuery(id+"F12.imprint","IMPRINT",EDGE,{"derivedFrom":subQ18}),-1.0]])]})]);}
            var Q1;
            Q1=makeQuery(id+"F5.boolean.opBoolean","SPLIT",FACE,{"disambiguationData":[TD([makeQuery(id+"F5.opExtrude","SWEPT_FACE",FACE,{"disambiguationData":[OSD([sQuery(id+"F4.wireOp",EDGE,"E41")])]})])],"derivedFrom":makeQuery(id+"F3.boolean.opBoolean","COPY",FACE,{"derivedFrom":makeQuery(id+"F3.opExtrude","CAP_FACE",FACE,{"disambiguationData":[OSD([sQuery(id+"F0.wireOp",EDGE,"E25.0"),sQuery(id+"F0.wireOp",EDGE,"E25.1"),sQuery(id+"F0.wireOp",EDGE,"E25.2"),sQuery(id+"F0.wireOp",EDGE,"E25.3"),sQuery(id+"F0.wireOp",EDGE,"E25.4"),sQuery(id+"F0.wireOp",EDGE,"E25.5"),sQuery(id+"F0.wireOp",EDGE,"E25.6"),sQuery(id+"F0.wireOp",EDGE,"E25.7")])],"isStart":false})})});
            extrude(context, id + "F13", {"entities" : qUnion([Q0]), "operationType" : NewBodyOperationType.REMOVE, "endBound" : BoundingType.UP_TO_SURFACE, "endBoundEntityFace" : qUnion([Q1]), "depth" : 25 * mm});
        }
        {
            var Q0;
            Q0=makeQuery(id+"F3.boolean.opBoolean","COPY",EDGE,{"derivedFrom":makeQuery(id+"F3.opExtrude","CAP_EDGE",EDGE,{"disambiguationData":[OSD([sQuery(id+"F0.wireOp",EDGE,"E25.6")])],"isStart":false})});
            var Q1;
            Q1=makeQuery(id+"F8.boolean.opBoolean","INTERSECT",EDGE,{"derivedFrom":[makeQuery(id+"F5.opExtrude","SWEPT_FACE",FACE,{"disambiguationData":[OSD([sQuery(id+"F4.wireOp",EDGE,"E30")])]}),makeQuery(id+"F8.opExtrude","CAP_FACE",FACE,{"disambiguationData":[OSD([sQuery(id+"F7.wireOp",EDGE,"E67")])],"isStart":false})]});
            var Q2;
            Q2=makeQuery(id+"F8.boolean.opBoolean","INTERSECT",EDGE,{"disambiguationData":[OD(1.0)],"derivedFrom":[makeQuery(id+"F5.opExtrude","SWEPT_FACE",FACE,{"disambiguationData":[OSD([sQuery(id+"F4.wireOp",EDGE,"E30")])]}),makeQuery(id+"F8.opExtrude","SWEPT_FACE",FACE,{"disambiguationData":[OSD([sQuery(id+"F7.wireOp",EDGE,"E67")])]})]});
            var Q3;
            {var subQ0=sQuery(id+"F4.wireOp",EDGE,"E30");Q3=makeQuery(id+"F8.boolean.opBoolean","SPLIT",EDGE,{"disambiguationData":[TD([makeQuery(id+"F5.opExtrude","SWEPT_FACE",FACE,{"disambiguationData":[OSD([sQuery(id+"F4.wireOp",EDGE,"E35.filletArc")])]})])],"derivedFrom":makeQuery(id+"F5.opExtrude","CAP_EDGE",EDGE,{"disambiguationData":[OSD([subQ0])],"isStart":false})});}
            var Q4;
            {var subQ0=sQuery(id+"F0.wireOp",EDGE,"E25.7");var subQ1=sQuery(id+"F0.wireOp",EDGE,"E25.1");var subQ2=sQuery(id+"F0.wireOp",EDGE,"E25.6");var subQ3=sQuery(id+"F0.wireOp",EDGE,"E25.5");var subQ4=sQuery(id+"F0.wireOp",EDGE,"E25.4");var subQ5=sQuery(id+"F0.wireOp",EDGE,"E25.0");var subQ6=sQuery(id+"F0.wireOp",EDGE,"E25.2");var subQ7=sQuery(id+"F0.wireOp",EDGE,"E25.3");Q4=makeQuery(id+"F8.boolean.opBoolean","INTERSECT",EDGE,{"derivedFrom":[makeQuery(id+"F5.boolean.opBoolean","SPLIT",FACE,{"disambiguationData":[TD([makeQuery(id+"F2.opExtrude","SWEPT_FACE",FACE,{"disambiguationData":[OSD([subQ5])]})])],"derivedFrom":makeQuery(id+"F3.boolean.opBoolean","COPY",FACE,{"derivedFrom":makeQuery(id+"F3.opExtrude","CAP_FACE",FACE,{"disambiguationData":[OSD([subQ5,subQ1,subQ6,subQ7,subQ4,subQ3,subQ2,subQ0])],"isStart":false})})}),makeQuery(id+"F8.opExtrude","SWEPT_FACE",FACE,{"disambiguationData":[OSD([sQuery(id+"F7.wireOp",EDGE,"E67")])]})]});}
            var Q5;
            Q5=makeQuery(id+"F8.boolean.opBoolean","INTERSECT",EDGE,{"disambiguationData":[OD(0.0)],"derivedFrom":[makeQuery(id+"F5.opExtrude","SWEPT_FACE",FACE,{"disambiguationData":[OSD([sQuery(id+"F4.wireOp",EDGE,"E30")])]}),makeQuery(id+"F8.opExtrude","SWEPT_FACE",FACE,{"disambiguationData":[OSD([sQuery(id+"F7.wireOp",EDGE,"E67")])]})]});
            fillet(context, id + "F14", {"entities" : qUnion([Q0, Q1, Q2, Q3, Q4, Q5]), "radius" : 3 * mm, "tangentPropagation" : true, "allowEdgeOverflow" : false});
        }
        {
            var Q0;
            Q0=makeQuery(id+"F1.opExtrude","CAP_EDGE",EDGE,{"disambiguationData":[OSD([sQuery(id+"F0.wireOp",EDGE,"E1.bottom")])],"isStart":false});
            fillet(context, id + "F15", {"entities" : qUnion([Q0]), "radius" : 2 * mm, "tangentPropagation" : true, "allowEdgeOverflow" : false});
        }
        {
            var Q0;
            {var subQ0=sQuery(id+"F0.wireOp",EDGE,"E21.filletArc");var subQ1=sQuery(id+"F0.wireOp",EDGE,"E7");var subQ2=sQuery(id+"F0.wireOp",EDGE,"E6");var subQ3=sQuery(id+"F0.wireOp",EDGE,"E5");var subQ4=sQuery(id+"F0.wireOp",EDGE,"E4");var subQ5=sQuery(id+"F0.wireOp",EDGE,"E22.filletArc");var subQ6=sQuery(id+"F0.wireOp",EDGE,"E1.bottom");var subQ7=sQuery(id+"F0.wireOp",EDGE,"E1.right");var subQ8=sQuery(id+"F0.wireOp",EDGE,"E1.top");var subQ9=sQuery(id+"F0.wireOp",EDGE,"E1.left");var subQ10=sQuery(id+"F0.wireOp",EDGE,"E23.filletArc");var subQ11=sQuery(id+"F0.wireOp",EDGE,"E24.filletArc");Q0=makeQuery(id+"F2.boolean.opBoolean","SPLIT",FACE,{"disambiguationData":[TD([makeQuery(id+"F1.opExtrude","SWEPT_FACE",FACE,{"disambiguationData":[OSD([subQ6])]})])],"derivedFrom":makeQuery(id+"F1.opExtrude","CAP_FACE",FACE,{"disambiguationData":[OSD([subQ6,subQ8,subQ9,subQ7,subQ4,subQ3,subQ2,subQ1,subQ0,subQ5,subQ10,subQ11])],"isStart":true})});}
            var sketch = newSketch(context, id + "F16", { "sketchPlane" : qUnion([Q0])});
            skLineSegment(sketch, "E79", {"start": v(-27.73, 74.25) * mm, "end": v(-15, 86.98) * mm});
            skLineSegment(sketch, "E80", {"start": v(27.73, 74.25) * mm, "end": v(15, 86.98) * mm});
            skLineSegment(sketch, "E81", {"start": v(-15, 86.98) * mm, "end": v(-15, 98.98) * mm});
            skLineSegment(sketch, "E82", {"start": v(15, 86.98) * mm, "end": v(15, 98.98) * mm});
            skArc(sketch, "E83", {"start": v(15, 98.98) * mm, "mid": v(0, 113.98) * mm, "end": v(-15, 98.98) * mm});
            skCircle(sketch, "E84", {"center": v(0, 98.98) * mm, "radius": 6 * mm});
            skLineSegment(sketch, "E85", {"start": v(0, 0) * mm, "end": v(-74.25, 0) * mm, "construction": true});
            skLineSegment(sketch, "E86", {"start": v(-74.25, 0) * mm, "end": v(74.25, 0) * mm, "construction": true});
            skLineSegment(sketch, "E87.MirrorCS", {"start": v(-15, -86.98) * mm, "end": v(-15, -98.98) * mm});
            skLineSegment(sketch, "E88.MirrorCS", {"start": v(-27.73, -74.25) * mm, "end": v(-15, -86.98) * mm});
            skLineSegment(sketch, "E89.MirrorCS", {"start": v(27.73, -74.25) * mm, "end": v(15, -86.98) * mm});
            skLineSegment(sketch, "E90.MirrorCS", {"start": v(15, -86.98) * mm, "end": v(15, -98.98) * mm});
            skArc(sketch, "E91.MirrorCS", {"start": v(15, -98.98) * mm, "mid": v(0, -113.98) * mm, "end": v(-15, -98.98) * mm});
            skCircle(sketch, "E92.MirrorC", {"center": v(0, -98.98) * mm, "radius": 6 * mm});
            skSolve(sketch);
        }
        {
            var Q0;
            Q0=makeQuery(id+"F16.imprint","IMPRINT",FACE,{"disambiguationData":[TD([[makeQuery(id+"F16.imprint","IMPRINT",EDGE,{"derivedFrom":makeQuery(id+"F1.opExtrude","CAP_EDGE",EDGE,{"disambiguationData":[OSD([sQuery(id+"F0.wireOp",EDGE,"E1.left")])],"isStart":true})}),-1.0]])]});
            var Q1;
            {var subQ0=sQuery(id+"F16.wireOp",EDGE,"E79");Q1=makeQuery(id+"F16.imprint","IMPRINT",FACE,{"disambiguationData":[TD([[makeQuery(id+"F16.imprint","IMPRINT",EDGE,{"derivedFrom":subQ0}),-1.0]])]});}
            var Q2;
            Q2=makeQuery(id+"F16.imprint","IMPRINT",FACE,{"disambiguationData":[TD([[makeQuery(id+"F16.imprint","IMPRINT",EDGE,{"derivedFrom":sQuery(id+"F16.wireOp",EDGE,"E87.MirrorCS")}),1.0]])]});
            extrude(context, id + "F17", {"entities" : qUnion([Q0, Q1, Q2]), "operationType" : NewBodyOperationType.ADD, "depth" : 5 * mm, "offsetDistance" : 25 * mm});
        }
    });
